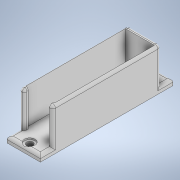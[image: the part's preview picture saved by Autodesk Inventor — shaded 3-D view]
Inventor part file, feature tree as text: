
AUTODESK INVENTOR PART (.ipt)
format: ipt  version: 2020 (Build 240168000, 168)  size: 176,640 bytes
history: native  units: in
note: dims shown in document units (in); Inventor stores cm internally (conversion verified against a paired STEP export)
features: sketch x3, extrude x2, fillet x2, hole x1
ambient origin geometry x8: Origin, YZ Plane, XZ Plane, XY Plane, X Axis, Y Axis, Z Axis, Center Point
bodies: Solid1 (feature_tree)
feature tree (8):
  extrude  "Extrusion1"  Depth=5.5in
  hole  "Hole1"  [1 undecoded]
  extrude  "Extrusion2"  Depth=1.2047in
  fillet  "Fillet1"  Radius=4.1339in
  fillet  "Fillet2"  Radius=0.5in
  sketch  "Sketch1"  dims[d0=1.378in d1=5.5in]
  sketch  "Sketch2"  dims[d2=0.25in d3=0.0in d4=0.25in]
  sketch  "Sketch3"  dims[d5=0.25in d6=0.266in d7=0.75in d8=0.438in d9=0.0625in d10=0.5635in d11=1.0in d12=0.8108in d13=1.2047in d14=4.1339in d15=0.5in d16=0.5in d17=1.0in d18=1.5in d19=0.0in d20=0.125in d21=0.125in]
note: 1 required parameter value undecoded (feature->parameter linkage not recoverable at this tier; creation-order binding heuristic only, values carry confidence <= 0.55)
